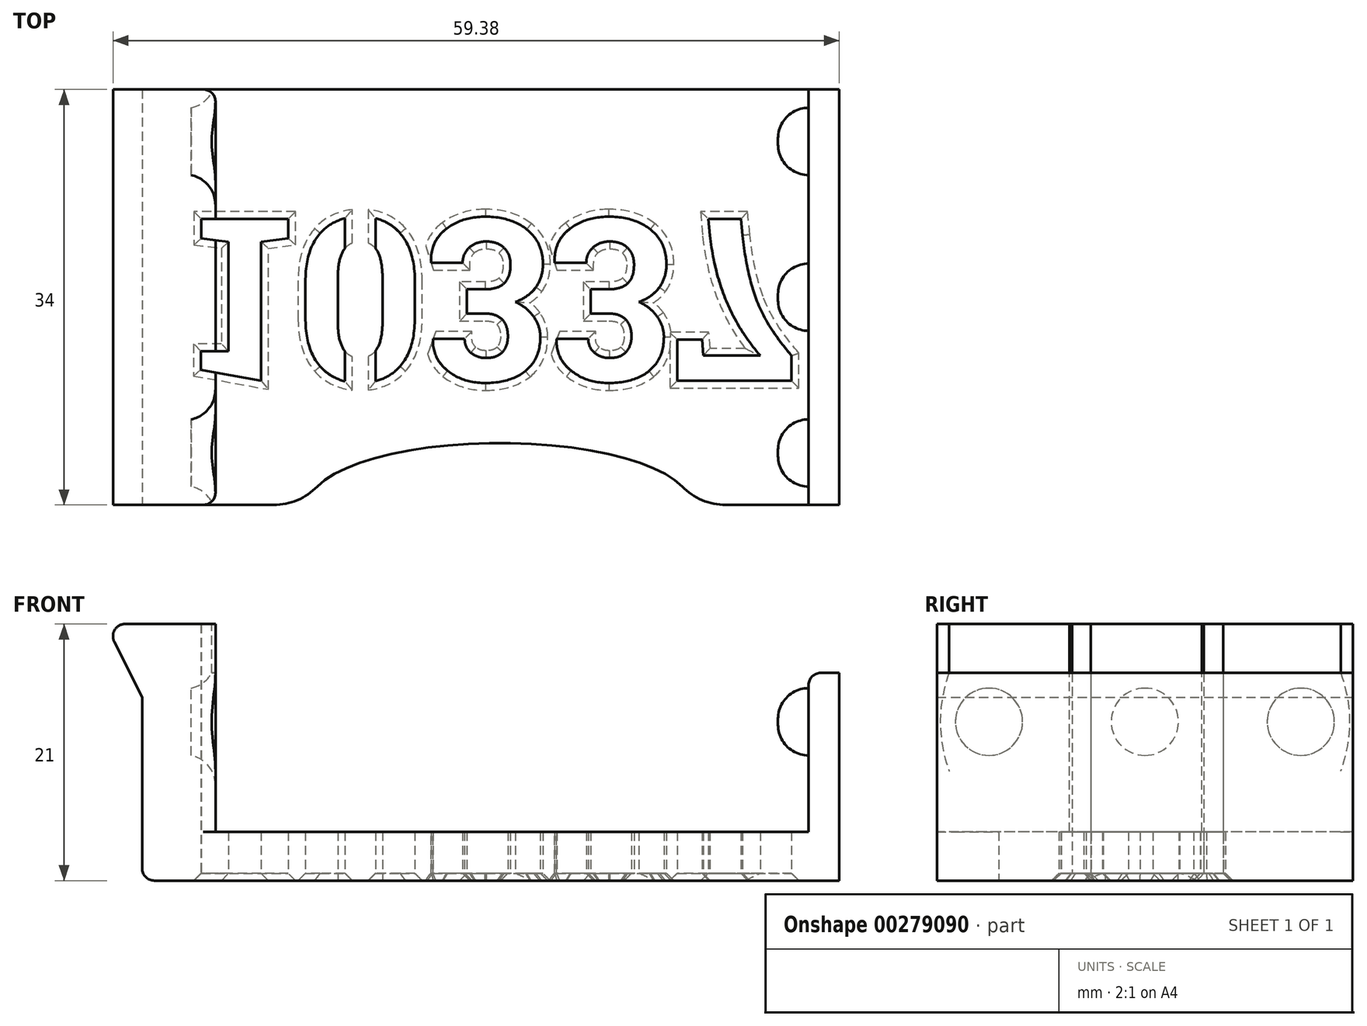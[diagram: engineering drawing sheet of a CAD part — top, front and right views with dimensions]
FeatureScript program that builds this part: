
annotation { "Feature Type Name" : "Feature", "Feature Type Description" : "" }
export const myFeature = defineFeature(function(context is Context, id is Id, definition is map)
    precondition{}
    {
        {
            var Q0;
            Q0=qCreatedBy(makeId("Top.planeOp"),FACE);
            var sketch = newSketch(context, id + "F0", { "sketchPlane" : qUnion([Q0])});
            skLineSegment(sketch, "E0.bottom", {"start": v(-29.25, 25.5) * mm, "end": v(29.25, 25.5) * mm});
            skLineSegment(sketch, "E0.top", {"start": v(-29.25, -25.5) * mm, "end": v(29.25, -25.5) * mm});
            skLineSegment(sketch, "E0.left", {"start": v(-29.25, 25.5) * mm, "end": v(-29.25, -25.5) * mm});
            skLineSegment(sketch, "E0.right", {"start": v(29.25, 25.5) * mm, "end": v(29.25, -25.5) * mm});
            skPoint(sketch, "E0.middle", {"position": v(0, 0) * mm});
            skSolve(sketch);
        }
        {
            var Q0;
            Q0 = qSketchRegion(id + "F0", true);
            extrude(context, id + "F1", {"entities" : qUnion([Q0]), "depth" : 4 * mm});
        }
        {
            var Q0;
            Q0=makeQuery(id+"F1.opExtrude","CAP_FACE",FACE,{"disambiguationData":[OSD([sQuery(id+"F0.wireOp",EDGE,"E0.bottom"),sQuery(id+"F0.wireOp",EDGE,"E0.top"),sQuery(id+"F0.wireOp",EDGE,"E0.left"),sQuery(id+"F0.wireOp",EDGE,"E0.right")])],"isStart":false});
            var sketch = newSketch(context, id + "F2", { "sketchPlane" : qUnion([Q0])});
            skLineSegment(sketch, "E1.bottom", {"start": v(-25.25, 25.5) * mm, "end": v(25.25, 25.5) * mm});
            skLineSegment(sketch, "E1.top", {"start": v(-25.25, -25.5) * mm, "end": v(25.25, -25.5) * mm});
            skLineSegment(sketch, "E1.left", {"start": v(-25.25, 25.5) * mm, "end": v(-25.25, -25.5) * mm});
            skLineSegment(sketch, "E1.right", {"start": v(25.25, 25.5) * mm, "end": v(25.25, -25.5) * mm});
            skPoint(sketch, "E1.middle", {"position": v(0, 0) * mm});
            skSolve(sketch);
        }
        {
            var Q0;
            {var subQ0=sQuery(id+"F2.wireOp",EDGE,"E1.left");Q0=makeQuery(id+"F2.imprint","IMPRINT",FACE,{"disambiguationData":[TD([[makeQuery(id+"F2.imprint","IMPRINT",EDGE,{"derivedFrom":subQ0}),-1.0]])]});}
            var Q1;
            {var subQ0=sQuery(id+"F2.wireOp",EDGE,"E1.right");Q1=makeQuery(id+"F2.imprint","IMPRINT",FACE,{"disambiguationData":[TD([[makeQuery(id+"F2.imprint","IMPRINT",EDGE,{"derivedFrom":subQ0}),1.0]])]});}
            extrude(context, id + "F3", {"entities" : qUnion([Q0, Q1]), "operationType" : NewBodyOperationType.ADD, "depth" : 13 * mm});
        }
        {
            var Q0;
            Q0=makeQuery(id+"F3.opExtrude","SWEPT_FACE",FACE,{"disambiguationData":[OSD([sQuery(id+"F2.wireOp",EDGE,"E1.left")])]});
            var sketch = newSketch(context, id + "F4", { "sketchPlane" : qUnion([Q0])});
            skLineSegment(sketch, "E2", {"start": v(0, 4) * mm, "end": v(0, 13) * mm});
            skPoint(sketch, "E2.endSnap0", {"position": v(0, 4) * mm});
            skLineSegment(sketch, "E3", {"start": v(0, 13) * mm, "end": v(25.5, 13) * mm});
            skLineSegment(sketch, "E4", {"start": v(0, 13) * mm, "end": v(-25.5, 13) * mm});
            skCircle(sketch, "E5", {"center": v(12.75, 13) * mm, "radius": 2.75 * mm});
            skCircle(sketch, "E6", {"center": v(0, 13) * mm, "radius": 2.75 * mm});
            skCircle(sketch, "E7", {"center": v(-12.75, 13) * mm, "radius": 2.75 * mm});
            skSolve(sketch);
        }
        {
            var Q0;
            {var subQ0=sQuery(id+"F4.wireOp",EDGE,"E5");var subQ1=sQuery(id+"F4.wireOp",EDGE,"E3");var subQ2=makeQuery(id+"F4.imprint","INTERSECT",VERTEX,{"disambiguationData":[OD(0.0)],"derivedFrom":[subQ1,subQ0]});Q0=makeQuery(id+"F4.imprint","IMPRINT",FACE,{"disambiguationData":[TD([[makeQuery(id+"F4.imprint","IMPRINT",EDGE,{"disambiguationData":[TD([[subQ2,-1.0]])],"derivedFrom":subQ1}),1.0]])]});}
            var Q1;
            {var subQ0=sQuery(id+"F4.wireOp",EDGE,"E5");var subQ1=sQuery(id+"F4.wireOp",EDGE,"E3");var subQ2=makeQuery(id+"F4.imprint","INTERSECT",VERTEX,{"disambiguationData":[OD(0.0)],"derivedFrom":[subQ1,subQ0]});Q1=makeQuery(id+"F4.imprint","IMPRINT",FACE,{"disambiguationData":[TD([[makeQuery(id+"F4.imprint","IMPRINT",EDGE,{"disambiguationData":[TD([[subQ2,-1.0]])],"derivedFrom":subQ1}),-1.0]])]});}
            var Q2;
            {var subQ1=sQuery(id+"F4.wireOp",EDGE,"E2");var subQ3=sQuery(id+"F4.wireOp",EDGE,"E6");var subQ4=makeQuery(id+"F4.imprint","INTERSECT",VERTEX,{"derivedFrom":[subQ1,subQ3]});Q2=makeQuery(id+"F4.imprint","IMPRINT",FACE,{"disambiguationData":[TD([[makeQuery(id+"F4.imprint","IMPRINT",EDGE,{"disambiguationData":[TD([[subQ4,-1.0]])],"derivedFrom":subQ3}),1.0]])]});}
            var Q3;
            {var subQ1=sQuery(id+"F4.wireOp",EDGE,"E3");var subQ3=sQuery(id+"F4.wireOp",EDGE,"E6");var subQ4=makeQuery(id+"F4.imprint","INTERSECT",VERTEX,{"derivedFrom":[subQ1,subQ3]});Q3=makeQuery(id+"F4.imprint","IMPRINT",FACE,{"disambiguationData":[TD([[makeQuery(id+"F4.imprint","IMPRINT",EDGE,{"disambiguationData":[TD([[subQ4,-1.0]])],"derivedFrom":subQ3}),1.0]])]});}
            var Q4;
            {var subQ1=sQuery(id+"F4.wireOp",EDGE,"E2");var subQ3=sQuery(id+"F4.wireOp",EDGE,"E6");var subQ4=makeQuery(id+"F4.imprint","INTERSECT",VERTEX,{"derivedFrom":[subQ1,subQ3]});Q4=makeQuery(id+"F4.imprint","IMPRINT",FACE,{"disambiguationData":[TD([[makeQuery(id+"F4.imprint","IMPRINT",EDGE,{"disambiguationData":[TD([[subQ4,1.0]])],"derivedFrom":subQ3}),1.0]])]});}
            var Q5;
            {var subQ0=sQuery(id+"F4.wireOp",EDGE,"E7");var subQ1=sQuery(id+"F4.wireOp",EDGE,"E4");var subQ2=makeQuery(id+"F4.imprint","INTERSECT",VERTEX,{"disambiguationData":[OD(0.0)],"derivedFrom":[subQ1,subQ0]});Q5=makeQuery(id+"F4.imprint","IMPRINT",FACE,{"disambiguationData":[TD([[makeQuery(id+"F4.imprint","IMPRINT",EDGE,{"disambiguationData":[TD([[subQ2,-1.0]])],"derivedFrom":subQ1}),1.0]])]});}
            var Q6;
            {var subQ0=sQuery(id+"F4.wireOp",EDGE,"E7");var subQ1=sQuery(id+"F4.wireOp",EDGE,"E4");var subQ2=makeQuery(id+"F4.imprint","INTERSECT",VERTEX,{"disambiguationData":[OD(0.0)],"derivedFrom":[subQ1,subQ0]});Q6=makeQuery(id+"F4.imprint","IMPRINT",FACE,{"disambiguationData":[TD([[makeQuery(id+"F4.imprint","IMPRINT",EDGE,{"disambiguationData":[TD([[subQ2,-1.0]])],"derivedFrom":subQ1}),-1.0]])]});}
            extrude(context, id + "F5", {"entities" : qUnion([Q0, Q1, Q2, Q3, Q4, Q5, Q6]), "operationType" : NewBodyOperationType.ADD, "depth" : 2 * mm});
        }
        {
            var Q0;
            Q0=makeQuery(id+"F3.opExtrude","SWEPT_FACE",FACE,{"disambiguationData":[OSD([sQuery(id+"F2.wireOp",EDGE,"E1.right")])]});
            var sketch = newSketch(context, id + "F6", { "sketchPlane" : qUnion([Q0])});
            skLineSegment(sketch, "E8", {"start": v(0, 4) * mm, "end": v(0, 13) * mm});
            skPoint(sketch, "E8.endSnap0", {"position": v(0, 4) * mm});
            skLineSegment(sketch, "E9", {"start": v(0, 13) * mm, "end": v(25.5, 13) * mm});
            skLineSegment(sketch, "E10", {"start": v(0, 13) * mm, "end": v(-25.5, 13) * mm});
            skCircle(sketch, "E11", {"center": v(0, 13) * mm, "radius": 2.75 * mm});
            skCircle(sketch, "E12", {"center": v(12.75, 13) * mm, "radius": 2.75 * mm});
            skCircle(sketch, "E13", {"center": v(-12.75, 13) * mm, "radius": 2.75 * mm});
            skSolve(sketch);
        }
        {
            var Q0;
            Q0 = qSketchRegion(id + "F6", true);
            extrude(context, id + "F7", {"entities" : qUnion([Q0]), "operationType" : NewBodyOperationType.ADD, "depth" : 2.5 * mm});
        }
        {
            var Q0;
            Q0=makeQuery(id+"F5.opExtrude","CAP_EDGE",EDGE,{"disambiguationData":[OSD([sQuery(id+"F4.wireOp",EDGE,"E5")])],"isStart":false});
            var Q1;
            Q1=makeQuery(id+"F5.opExtrude","CAP_EDGE",EDGE,{"disambiguationData":[OSD([sQuery(id+"F4.wireOp",EDGE,"E6")])],"isStart":false});
            var Q2;
            Q2=makeQuery(id+"F5.opExtrude","CAP_EDGE",EDGE,{"disambiguationData":[OSD([sQuery(id+"F4.wireOp",EDGE,"E7")])],"isStart":false});
            var Q3;
            Q3=makeQuery(id+"F7.opExtrude","CAP_FACE",FACE,{"disambiguationData":[OSD([sQuery(id+"F6.wireOp",EDGE,"E12")])],"isStart":false});
            var Q4;
            Q4=makeQuery(id+"F7.opExtrude","CAP_FACE",FACE,{"disambiguationData":[OSD([sQuery(id+"F6.wireOp",EDGE,"E11")])],"isStart":false});
            var Q5;
            Q5=makeQuery(id+"F7.opExtrude","CAP_FACE",FACE,{"disambiguationData":[OSD([sQuery(id+"F6.wireOp",EDGE,"E13")])],"isStart":false});
            fillet(context, id + "F8", {"entities" : qUnion([Q0, Q1, Q2, Q3, Q4, Q5]), "radius" : 2.5 * mm, "tangentPropagation" : true, "allowEdgeOverflow" : false});
        }
        {
            var Q0;
            {var subQ0=sQuery(id+"F0.wireOp",EDGE,"E0.top");var subQ1=makeQuery(id+"F1.opExtrude","CAP_EDGE",EDGE,{"disambiguationData":[OSD([subQ0])],"isStart":false});Q0=makeQuery(id+"F3.boolean.opBoolean","MERGE",FACE,{"derivedFrom":[makeQuery(id+"F1.opExtrude","SWEPT_FACE",FACE,{"disambiguationData":[OSD([subQ0])]}),makeQuery(id+"F3.opExtrude","SWEPT_FACE",FACE,{"disambiguationData":[OSD([subQ0]),TDD([makeQuery(id+"F2.imprint","IMPRINT",EDGE,{"disambiguationData":[TD([[makeQuery(id+"F2.imprint","INTERSECT",VERTEX,{"derivedFrom":[subQ1,makeQuery(id+"F1.opExtrude","CAP_EDGE",EDGE,{"disambiguationData":[OSD([sQuery(id+"F0.wireOp",EDGE,"E0.left")])],"isStart":false})]}),-1.0]])],"derivedFrom":subQ1})])]}),makeQuery(id+"F3.opExtrude","SWEPT_FACE",FACE,{"disambiguationData":[OSD([subQ0]),TDD([makeQuery(id+"F2.imprint","IMPRINT",EDGE,{"disambiguationData":[TD([[makeQuery(id+"F2.imprint","INTERSECT",VERTEX,{"derivedFrom":[subQ1,makeQuery(id+"F1.opExtrude","CAP_EDGE",EDGE,{"disambiguationData":[OSD([sQuery(id+"F0.wireOp",EDGE,"E0.right")])],"isStart":false})]}),1.0]])],"derivedFrom":subQ1})])]})]});}
            var sketch = newSketch(context, id + "F9", { "sketchPlane" : qUnion([Q0])});
            skLineSegment(sketch, "E14.bottom", {"start": v(29.25, 17) * mm, "end": v(27.75, 17) * mm});
            skLineSegment(sketch, "E14.top", {"start": v(29.25, 0) * mm, "end": v(27.75, 0) * mm});
            skLineSegment(sketch, "E14.left", {"start": v(29.25, 17) * mm, "end": v(29.25, 0) * mm});
            skLineSegment(sketch, "E14.right", {"start": v(27.75, 17) * mm, "end": v(27.75, 0) * mm});
            skSolve(sketch);
        }
        {
            var Q0;
            Q0 = qSketchRegion(id + "F9", true);
            extrude(context, id + "F10", {"entities" : qUnion([Q0]), "operationType" : NewBodyOperationType.REMOVE, "endBound" : BoundingType.THROUGH_ALL, "oppositeDirection" : true, "depth" : 25 * mm});
        }
        {
            var Q0;
            Q0=makeQuery(id+"F3.opExtrude","CAP_FACE",FACE,{"disambiguationData":[OSD([sQuery(id+"F0.wireOp",EDGE,"E0.bottom"),sQuery(id+"F0.wireOp",EDGE,"E0.top"),sQuery(id+"F0.wireOp",EDGE,"E0.left"),sQuery(id+"F2.wireOp",EDGE,"E1.left")])],"isStart":false});
            extrude(context, id + "F11", {"entities" : qUnion([Q0]), "operationType" : NewBodyOperationType.ADD, "depth" : 4 * mm});
        }
        {
            var Q0;
            {var subQ0=sQuery(id+"F0.wireOp",EDGE,"E0.left");Q0=makeQuery(id+"F11.boolean.opBoolean","MERGE",FACE,{"derivedFrom":[makeQuery(id+"F3.boolean.opBoolean","MERGE",FACE,{"derivedFrom":[makeQuery(id+"F1.opExtrude","SWEPT_FACE",FACE,{"disambiguationData":[OSD([subQ0])]}),makeQuery(id+"F3.opExtrude","SWEPT_FACE",FACE,{"disambiguationData":[OSD([subQ0])]})]}),makeQuery(id+"F11.opExtrude","SWEPT_FACE",FACE,{"disambiguationData":[OSD([subQ0])]})]});}
            var sketch = newSketch(context, id + "F12", { "sketchPlane" : qUnion([Q0])});
            skLineSegment(sketch, "E15.bottom", {"start": v(25.5, 21) * mm, "end": v(-25.5, 21) * mm});
            skLineSegment(sketch, "E15.top", {"start": v(25.5, 15) * mm, "end": v(-25.5, 15) * mm});
            skLineSegment(sketch, "E15.left", {"start": v(25.5, 21) * mm, "end": v(25.5, 15) * mm});
            skLineSegment(sketch, "E15.right", {"start": v(-25.5, 21) * mm, "end": v(-25.5, 15) * mm});
            skSolve(sketch);
        }
        {
            var Q0;
            Q0 = qSketchRegion(id + "F12", true);
            extrude(context, id + "F13", {"entities" : qUnion([Q0]), "operationType" : NewBodyOperationType.ADD, "depth" : 3 * mm});
        }
        {
            var Q0;
            {var subQ0=sQuery(id+"F0.wireOp",EDGE,"E0.top");var subQ1=makeQuery(id+"F1.opExtrude","CAP_EDGE",EDGE,{"disambiguationData":[OSD([subQ0])],"isStart":false});Q0=makeQuery(id+"F13.boolean.opBoolean","MERGE",FACE,{"derivedFrom":[makeQuery(id+"F11.boolean.opBoolean","MERGE",FACE,{"derivedFrom":[makeQuery(id+"F3.boolean.opBoolean","MERGE",FACE,{"derivedFrom":[makeQuery(id+"F1.opExtrude","SWEPT_FACE",FACE,{"disambiguationData":[OSD([subQ0])]}),makeQuery(id+"F3.opExtrude","SWEPT_FACE",FACE,{"disambiguationData":[OSD([subQ0]),TDD([makeQuery(id+"F2.imprint","IMPRINT",EDGE,{"disambiguationData":[TD([[makeQuery(id+"F2.imprint","INTERSECT",VERTEX,{"derivedFrom":[subQ1,makeQuery(id+"F1.opExtrude","CAP_EDGE",EDGE,{"disambiguationData":[OSD([sQuery(id+"F0.wireOp",EDGE,"E0.left")])],"isStart":false})]}),-1.0]])],"derivedFrom":subQ1})])]}),makeQuery(id+"F3.opExtrude","SWEPT_FACE",FACE,{"disambiguationData":[OSD([subQ0]),TDD([makeQuery(id+"F2.imprint","IMPRINT",EDGE,{"disambiguationData":[TD([[makeQuery(id+"F2.imprint","INTERSECT",VERTEX,{"derivedFrom":[subQ1,makeQuery(id+"F1.opExtrude","CAP_EDGE",EDGE,{"disambiguationData":[OSD([sQuery(id+"F0.wireOp",EDGE,"E0.right")])],"isStart":false})]}),1.0]])],"derivedFrom":subQ1})])]})]}),makeQuery(id+"F11.opExtrude","SWEPT_FACE",FACE,{"disambiguationData":[OSD([subQ0])]})]}),makeQuery(id+"F13.opExtrude","SWEPT_FACE",FACE,{"disambiguationData":[OSD([sQuery(id+"F12.wireOp",EDGE,"E15.left")])]})]});}
            var sketch = newSketch(context, id + "F14", { "sketchPlane" : qUnion([Q0])});
            skLineSegment(sketch, "E16", {"start": v(-32.25, 21) * mm, "end": v(-29.25, 15) * mm});
            skLineSegment(sketch, "E17", {"start": v(-32.25, 21) * mm, "end": v(-25.25, 18) * mm});
            skPoint(sketch, "E17.endSnap0", {"position": v(-30.75, 18) * mm});
            skSolve(sketch);
        }
        {
            var Q0;
            Q0=makeQuery(id+"F14.imprint","IMPRINT",FACE,{"disambiguationData":[TD([[makeQuery(id+"F14.imprint","IMPRINT",EDGE,{"derivedFrom":sQuery(id+"F14.wireOp",EDGE,"E16")}),-1.0]])]});
            var Q1;
            {var subQ0=sQuery(id+"F14.wireOp",EDGE,"E17");Q1=makeQuery(id+"F14.imprint","IMPRINT",FACE,{"disambiguationData":[TD([[makeQuery(id+"F14.imprint","IMPRINT",EDGE,{"derivedFrom":subQ0}),1.0]])]});}
            extrude(context, id + "F15", {"entities" : qUnion([Q0, Q1]), "operationType" : NewBodyOperationType.REMOVE, "endBound" : BoundingType.THROUGH_ALL, "oppositeDirection" : true, "depth" : 25 * mm});
        }
        {
            var Q0;
            {var subQ0=sQuery(id+"F0.wireOp",EDGE,"E0.top");var subQ1=makeQuery(id+"F1.opExtrude","CAP_EDGE",EDGE,{"disambiguationData":[OSD([subQ0])],"isStart":false});Q0=makeQuery(id+"F13.boolean.opBoolean","MERGE",FACE,{"derivedFrom":[makeQuery(id+"F11.boolean.opBoolean","MERGE",FACE,{"derivedFrom":[makeQuery(id+"F3.boolean.opBoolean","MERGE",FACE,{"derivedFrom":[makeQuery(id+"F1.opExtrude","SWEPT_FACE",FACE,{"disambiguationData":[OSD([subQ0])]}),makeQuery(id+"F3.opExtrude","SWEPT_FACE",FACE,{"disambiguationData":[OSD([subQ0]),TDD([makeQuery(id+"F2.imprint","IMPRINT",EDGE,{"disambiguationData":[TD([[makeQuery(id+"F2.imprint","INTERSECT",VERTEX,{"derivedFrom":[subQ1,makeQuery(id+"F1.opExtrude","CAP_EDGE",EDGE,{"disambiguationData":[OSD([sQuery(id+"F0.wireOp",EDGE,"E0.left")])],"isStart":false})]}),-1.0]])],"derivedFrom":subQ1})])]}),makeQuery(id+"F3.opExtrude","SWEPT_FACE",FACE,{"disambiguationData":[OSD([subQ0]),TDD([makeQuery(id+"F2.imprint","IMPRINT",EDGE,{"disambiguationData":[TD([[makeQuery(id+"F2.imprint","INTERSECT",VERTEX,{"derivedFrom":[subQ1,makeQuery(id+"F1.opExtrude","CAP_EDGE",EDGE,{"disambiguationData":[OSD([sQuery(id+"F0.wireOp",EDGE,"E0.right")])],"isStart":false})]}),1.0]])],"derivedFrom":subQ1})])]})]}),makeQuery(id+"F11.opExtrude","SWEPT_FACE",FACE,{"disambiguationData":[OSD([subQ0])]})]}),makeQuery(id+"F13.opExtrude","SWEPT_FACE",FACE,{"disambiguationData":[OSD([sQuery(id+"F12.wireOp",EDGE,"E15.left")])]})]});}
            extrude(context, id + "F16", {"entities" : qUnion([Q0]), "operationType" : NewBodyOperationType.REMOVE, "oppositeDirection" : true, "depth" : 8.5 * mm});
        }
        {
            var Q0;
            {var subQ0=sQuery(id+"F0.wireOp",EDGE,"E0.bottom");var subQ1=makeQuery(id+"F1.opExtrude","CAP_EDGE",EDGE,{"disambiguationData":[OSD([subQ0])],"isStart":false});Q0=makeQuery(id+"F13.boolean.opBoolean","MERGE",FACE,{"derivedFrom":[makeQuery(id+"F11.boolean.opBoolean","MERGE",FACE,{"derivedFrom":[makeQuery(id+"F3.boolean.opBoolean","MERGE",FACE,{"derivedFrom":[makeQuery(id+"F1.opExtrude","SWEPT_FACE",FACE,{"disambiguationData":[OSD([subQ0])]}),makeQuery(id+"F3.opExtrude","SWEPT_FACE",FACE,{"disambiguationData":[OSD([subQ0]),TDD([makeQuery(id+"F2.imprint","IMPRINT",EDGE,{"disambiguationData":[TD([[makeQuery(id+"F2.imprint","INTERSECT",VERTEX,{"derivedFrom":[subQ1,makeQuery(id+"F1.opExtrude","CAP_EDGE",EDGE,{"disambiguationData":[OSD([sQuery(id+"F0.wireOp",EDGE,"E0.left")])],"isStart":false})]}),-1.0]])],"derivedFrom":subQ1})])]}),makeQuery(id+"F3.opExtrude","SWEPT_FACE",FACE,{"disambiguationData":[OSD([subQ0]),TDD([makeQuery(id+"F2.imprint","IMPRINT",EDGE,{"disambiguationData":[TD([[makeQuery(id+"F2.imprint","INTERSECT",VERTEX,{"derivedFrom":[subQ1,makeQuery(id+"F1.opExtrude","CAP_EDGE",EDGE,{"disambiguationData":[OSD([sQuery(id+"F0.wireOp",EDGE,"E0.right")])],"isStart":false})]}),1.0]])],"derivedFrom":subQ1})])]})]}),makeQuery(id+"F11.opExtrude","SWEPT_FACE",FACE,{"disambiguationData":[OSD([subQ0])]})]}),makeQuery(id+"F13.opExtrude","SWEPT_FACE",FACE,{"disambiguationData":[OSD([sQuery(id+"F12.wireOp",EDGE,"E15.right")])]})]});}
            extrude(context, id + "F17", {"entities" : qUnion([Q0]), "operationType" : NewBodyOperationType.REMOVE, "oppositeDirection" : true, "depth" : 8.5 * mm});
        }
        {
            var Q0;
            {var subQ0=sQuery(id+"F24.wireOp",EDGE,"E21.right");var subQ1=sQuery(id+"F24.wireOp",EDGE,"E21.left");var subQ2=sQuery(id+"F22.wireOp",EDGE,"E19.sketch_text.stroke-27");var subQ3=sQuery(id+"F22.wireOp",EDGE,"E19.sketch_text.stroke-26");var subQ4=sQuery(id+"F22.wireOp",EDGE,"E19.sketch_text.stroke-22");var subQ5=sQuery(id+"F22.wireOp",EDGE,"E19.sketch_text.stroke-21");var subQ7=sQuery(id+"F2.wireOp",EDGE,"E1.left");var subQ9=sQuery(id+"F0.wireOp",EDGE,"E0.bottom");var subQ10=sQuery(id+"F0.wireOp",EDGE,"E0.top");var subQ12=makeQuery(id+"F1.opExtrude","CAP_FACE",FACE,{"disambiguationData":[OSD([subQ9,subQ10,sQuery(id+"F0.wireOp",EDGE,"E0.left"),sQuery(id+"F0.wireOp",EDGE,"E0.right")])],"isStart":false});Q0=makeQuery(id+"F25.boolean.opBoolean","MERGE",FACE,{"derivedFrom":[makeQuery(id+"F23.boolean.opBoolean","SPLIT",FACE,{"disambiguationData":[TD([makeQuery(id+"F23.opExtrude","SWEPT_FACE",FACE,{"disambiguationData":[OSD([sQuery(id+"F22.wireOp",EDGE,"E19.sketch_text.stroke-20")])]})])],"derivedFrom":subQ12}),makeQuery(id+"F23.boolean.opBoolean","SPLIT",FACE,{"disambiguationData":[TD([makeQuery(id+"F3.opExtrude","SWEPT_FACE",FACE,{"disambiguationData":[OSD([subQ7])]})])],"derivedFrom":subQ12}),makeQuery(id+"F25.opExtrude","CAP_FACE",FACE,{"disambiguationData":[OSD([subQ5,subQ4,sQuery(id+"F24.wireOp",EDGE,"E21.bottom"),subQ1,subQ0])],"isStart":false}),makeQuery(id+"F25.opExtrude","CAP_FACE",FACE,{"disambiguationData":[OSD([subQ3,subQ2,sQuery(id+"F24.wireOp",EDGE,"E21.top"),subQ1,subQ0])],"isStart":false})]});}
            var sketch = newSketch(context, id + "F18", { "sketchPlane" : qUnion([Q0])});
            skEllipse(sketch, "E18", {"center": v(0, -17.04) * mm, "majorRadius": 15.65 * mm, "minorRadius": 5.1 * mm, "majorAxis": v(1, 0)});
            skSolve(sketch);
        }
        {
            var Q0;
            Q0 = qSketchRegion(id + "F18", true);
            var Q1;
            {var subQ0=sQuery(id+"F18.wireOp",EDGE,"E18");var subQ1=sQuery(id+"F0.wireOp",EDGE,"E0.top");var subQ2=makeQuery(id+"F21.opFillet","BLEND_EDGE",EDGE,{"blendedFrom":[makeQuery(id+"F16.boolean.opBoolean","COPY",EDGE,{"derivedFrom":makeQuery(id+"F16.opExtrude","CAP_EDGE",EDGE,{"disambiguationData":[OSD([subQ1]),TDD([makeQuery(id+"F1.opExtrude","CAP_EDGE",EDGE,{"disambiguationData":[OSD([subQ1])],"isStart":false})])],"isStart":false})}),makeQuery(id+"F1.opExtrude","CAP_FACE",FACE,{"disambiguationData":[OSD([sQuery(id+"F0.wireOp",EDGE,"E0.bottom"),subQ1,sQuery(id+"F0.wireOp",EDGE,"E0.left"),sQuery(id+"F0.wireOp",EDGE,"E0.right")])],"isStart":false})],"blendedInto":[makeQuery(id+"F1.opExtrude","CAP_FACE",FACE,{"disambiguationData":[OSD([sQuery(id+"F0.wireOp",EDGE,"E0.bottom"),subQ1,sQuery(id+"F0.wireOp",EDGE,"E0.left"),sQuery(id+"F0.wireOp",EDGE,"E0.right")])],"isStart":false})]});var subQ3=makeQuery(id+"F18.imprint","INTERSECT",VERTEX,{"disambiguationData":[OD(0.0)],"derivedFrom":[subQ2,subQ0]});Q1=makeQuery(id+"F18.imprint","IMPRINT",FACE,{"disambiguationData":[TD([[makeQuery(id+"F18.imprint","IMPRINT",EDGE,{"disambiguationData":[TD([[subQ3,-1.0]])],"derivedFrom":subQ0}),1.0]])]});}
            extrude(context, id + "F19", {"entities" : qUnion([Q0, Q1]), "operationType" : NewBodyOperationType.REMOVE, "oppositeDirection" : true, "depth" : 25 * mm});
        }
        {
            var Q0;
            Q0=makeQuery(id+"F19.boolean.opBoolean","INTERSECT",EDGE,{"disambiguationData":[OD(1.0)],"derivedFrom":[makeQuery(id+"F16.boolean.opBoolean","COPY",FACE,{"derivedFrom":makeQuery(id+"F16.opExtrude","CAP_FACE",FACE,{"disambiguationData":[OSD([sQuery(id+"F0.wireOp",EDGE,"E0.top"),sQuery(id+"F12.wireOp",EDGE,"E15.left")])],"isStart":false})}),makeQuery(id+"F19.opExtrude","SWEPT_FACE",FACE,{"disambiguationData":[OSD([sQuery(id+"F18.wireOp",EDGE,"E18")])]})]});
            var Q1;
            Q1=makeQuery(id+"F19.boolean.opBoolean","INTERSECT",EDGE,{"disambiguationData":[OD(0.0)],"derivedFrom":[makeQuery(id+"F16.boolean.opBoolean","COPY",FACE,{"derivedFrom":makeQuery(id+"F16.opExtrude","CAP_FACE",FACE,{"disambiguationData":[OSD([sQuery(id+"F0.wireOp",EDGE,"E0.top"),sQuery(id+"F12.wireOp",EDGE,"E15.left")])],"isStart":false})}),makeQuery(id+"F19.opExtrude","SWEPT_FACE",FACE,{"disambiguationData":[OSD([sQuery(id+"F18.wireOp",EDGE,"E18")])]})]});
            fillet(context, id + "F20", {"entities" : qUnion([Q0, Q1]), "radius" : 5 * mm, "tangentPropagation" : true, "allowEdgeOverflow" : false});
        }
        {
            var Q0;
            {var subQ0=sQuery(id+"F14.wireOp",EDGE,"E17");var subQ1=sQuery(id+"F12.wireOp",EDGE,"E15.left");var subQ2=sQuery(id+"F12.wireOp",EDGE,"E15.bottom");var subQ3=sQuery(id+"F0.wireOp",EDGE,"E0.top");var subQ4=sQuery(id+"F14.wireOp",EDGE,"E16");Q0=makeQuery(id+"F15.boolean.opBoolean","MERGE",EDGE,{"derivedFrom":[makeQuery(id+"F13.opExtrude","CAP_EDGE",EDGE,{"disambiguationData":[OSD([subQ2])],"isStart":false}),makeQuery(id+"F15.opExtrude","SWEPT_EDGE",EDGE,{"disambiguationData":[OSD([subQ3,subQ2,subQ1,subQ4,subQ0]),ownerDisambiguation([makeQuery(id+"F15.opExtrude","SWEPT_BODY",BODY,{"disambiguationData":[OSD([subQ3,sQuery(id+"F0.wireOp",EDGE,"E0.left"),sQuery(id+"F12.wireOp",EDGE,"E15.top"),subQ1,subQ4])]})])]}),makeQuery(id+"F15.opExtrude","SWEPT_EDGE",EDGE,{"disambiguationData":[OSD([subQ3,subQ2,subQ1,subQ4,subQ0]),ownerDisambiguation([makeQuery(id+"F15.opExtrude","SWEPT_BODY",BODY,{"disambiguationData":[OSD([subQ3,sQuery(id+"F2.wireOp",EDGE,"E1.top"),sQuery(id+"F2.wireOp",EDGE,"E1.left"),subQ2,subQ1,subQ0])]})])]})]});}
            var Q1;
            Q1=makeQuery(id+"F15.boolean.opBoolean","COPY",EDGE,{"derivedFrom":makeQuery(id+"F15.opExtrude","SWEPT_EDGE",EDGE,{"disambiguationData":[OSD([sQuery(id+"F0.wireOp",EDGE,"E0.top"),sQuery(id+"F2.wireOp",EDGE,"E1.top"),sQuery(id+"F2.wireOp",EDGE,"E1.left"),sQuery(id+"F14.wireOp",EDGE,"E17")])]})});
            var Q2;
            Q2=makeQuery(id+"F3.opExtrude","CAP_EDGE",EDGE,{"disambiguationData":[OSD([sQuery(id+"F2.wireOp",EDGE,"E1.right")])],"isStart":false});
            var Q3;
            Q3=makeQuery(id+"F10.boolean.opBoolean","COPY",EDGE,{"derivedFrom":makeQuery(id+"F10.opExtrude","SWEPT_EDGE",EDGE,{"disambiguationData":[OSD([sQuery(id+"F0.wireOp",EDGE,"E0.top"),sQuery(id+"F9.wireOp",EDGE,"E14.bottom"),sQuery(id+"F9.wireOp",EDGE,"E14.right")])]})});
            var Q4;
            Q4=makeQuery(id+"F1.opExtrude","CAP_EDGE",EDGE,{"disambiguationData":[OSD([sQuery(id+"F0.wireOp",EDGE,"E0.left")])],"isStart":true});
            var Q5;
            Q5=makeQuery(id+"F10.boolean.opBoolean","COPY",EDGE,{"derivedFrom":makeQuery(id+"F10.opExtrude","SWEPT_EDGE",EDGE,{"disambiguationData":[OSD([sQuery(id+"F0.wireOp",EDGE,"E0.top"),sQuery(id+"F9.wireOp",EDGE,"E14.top"),sQuery(id+"F9.wireOp",EDGE,"E14.right")])]})});
            var Q6;
            Q6=makeQuery(id+"F1.opExtrude","CAP_EDGE",EDGE,{"disambiguationData":[OSD([sQuery(id+"F0.wireOp",EDGE,"E0.bottom")])],"isStart":true});
            var Q7;
            Q7=makeQuery(id+"F1.opExtrude","CAP_EDGE",EDGE,{"disambiguationData":[OSD([sQuery(id+"F0.wireOp",EDGE,"E0.top")])],"isStart":true});
            var Q8;
            {var subQ0=sQuery(id+"F0.wireOp",EDGE,"E0.bottom");Q8=makeQuery(id+"F17.boolean.opBoolean","COPY",EDGE,{"derivedFrom":makeQuery(id+"F17.opExtrude","CAP_EDGE",EDGE,{"disambiguationData":[OSD([subQ0]),TDD([makeQuery(id+"F1.opExtrude","CAP_EDGE",EDGE,{"disambiguationData":[OSD([subQ0])],"isStart":true})])],"isStart":false})});}
            var Q9;
            {var subQ0=sQuery(id+"F0.wireOp",EDGE,"E0.top");Q9=makeQuery(id+"F16.boolean.opBoolean","COPY",EDGE,{"derivedFrom":makeQuery(id+"F16.opExtrude","CAP_EDGE",EDGE,{"disambiguationData":[OSD([subQ0]),TDD([makeQuery(id+"F1.opExtrude","CAP_EDGE",EDGE,{"disambiguationData":[OSD([subQ0])],"isStart":true})])],"isStart":false})});}
            var Q10;
            Q10=makeQuery(id+"F16.boolean.opBoolean","COPY",EDGE,{"derivedFrom":makeQuery(id+"F16.opExtrude","CAP_EDGE",EDGE,{"disambiguationData":[OSD([sQuery(id+"F0.wireOp",EDGE,"E0.top"),sQuery(id+"F0.wireOp",EDGE,"E0.left")])],"isStart":false})});
            var Q11;
            Q11=makeQuery(id+"F16.boolean.opBoolean","COPY",EDGE,{"derivedFrom":makeQuery(id+"F16.opExtrude","CAP_EDGE",EDGE,{"disambiguationData":[OSD([sQuery(id+"F14.wireOp",EDGE,"E16")])],"isStart":false})});
            var Q12;
            Q12=makeQuery(id+"F17.boolean.opBoolean","COPY",EDGE,{"derivedFrom":makeQuery(id+"F17.opExtrude","CAP_EDGE",EDGE,{"disambiguationData":[OSD([sQuery(id+"F0.wireOp",EDGE,"E0.bottom"),sQuery(id+"F12.wireOp",EDGE,"E15.right"),sQuery(id+"F14.wireOp",EDGE,"E16")])],"isStart":false})});
            var Q13;
            Q13=makeQuery(id+"F17.boolean.opBoolean","COPY",EDGE,{"derivedFrom":makeQuery(id+"F17.opExtrude","CAP_EDGE",EDGE,{"disambiguationData":[OSD([sQuery(id+"F0.wireOp",EDGE,"E0.bottom"),sQuery(id+"F0.wireOp",EDGE,"E0.left")])],"isStart":false})});
            var Q14;
            Q14=makeQuery(id+"F17.boolean.opBoolean","COPY",EDGE,{"derivedFrom":makeQuery(id+"F17.opExtrude","CAP_EDGE",EDGE,{"disambiguationData":[OSD([sQuery(id+"F0.wireOp",EDGE,"E0.bottom"),sQuery(id+"F9.wireOp",EDGE,"E14.right")])],"isStart":false})});
            var Q15;
            Q15=makeQuery(id+"F16.boolean.opBoolean","COPY",EDGE,{"derivedFrom":makeQuery(id+"F16.opExtrude","CAP_EDGE",EDGE,{"disambiguationData":[OSD([sQuery(id+"F9.wireOp",EDGE,"E14.right")])],"isStart":false})});
            var Q16;
            Q16=makeQuery(id+"F17.boolean.opBoolean","COPY",EDGE,{"derivedFrom":makeQuery(id+"F17.opExtrude","CAP_EDGE",EDGE,{"disambiguationData":[OSD([sQuery(id+"F0.wireOp",EDGE,"E0.bottom"),sQuery(id+"F12.wireOp",EDGE,"E15.right"),sQuery(id+"F14.wireOp",EDGE,"E17")])],"isStart":false})});
            var Q17;
            Q17=makeQuery(id+"F17.boolean.opBoolean","COPY",EDGE,{"derivedFrom":makeQuery(id+"F17.opExtrude","CAP_EDGE",EDGE,{"disambiguationData":[OSD([sQuery(id+"F0.wireOp",EDGE,"E0.bottom"),sQuery(id+"F2.wireOp",EDGE,"E1.bottom"),sQuery(id+"F2.wireOp",EDGE,"E1.left")])],"isStart":false})});
            var Q18;
            Q18=makeQuery(id+"F16.boolean.opBoolean","COPY",EDGE,{"derivedFrom":makeQuery(id+"F16.opExtrude","CAP_EDGE",EDGE,{"disambiguationData":[OSD([sQuery(id+"F0.wireOp",EDGE,"E0.top"),sQuery(id+"F2.wireOp",EDGE,"E1.top"),sQuery(id+"F2.wireOp",EDGE,"E1.left")])],"isStart":false})});
            var Q19;
            Q19=makeQuery(id+"F16.boolean.opBoolean","COPY",EDGE,{"derivedFrom":makeQuery(id+"F16.opExtrude","CAP_EDGE",EDGE,{"disambiguationData":[OSD([sQuery(id+"F14.wireOp",EDGE,"E17")])],"isStart":false})});
            var Q20;
            Q20=makeQuery(id+"F16.boolean.opBoolean","COPY",EDGE,{"derivedFrom":makeQuery(id+"F16.opExtrude","CAP_EDGE",EDGE,{"disambiguationData":[OSD([sQuery(id+"F0.wireOp",EDGE,"E0.top"),sQuery(id+"F2.wireOp",EDGE,"E1.top"),sQuery(id+"F2.wireOp",EDGE,"E1.right")])],"isStart":false})});
            var Q21;
            {var subQ0=sQuery(id+"F0.wireOp",EDGE,"E0.top");Q21=makeQuery(id+"F16.boolean.opBoolean","COPY",EDGE,{"derivedFrom":makeQuery(id+"F16.opExtrude","CAP_EDGE",EDGE,{"disambiguationData":[OSD([subQ0]),TDD([makeQuery(id+"F1.opExtrude","CAP_EDGE",EDGE,{"disambiguationData":[OSD([subQ0])],"isStart":false})])],"isStart":false})});}
            var Q22;
            {var subQ0=sQuery(id+"F0.wireOp",EDGE,"E0.bottom");Q22=makeQuery(id+"F17.boolean.opBoolean","COPY",EDGE,{"derivedFrom":makeQuery(id+"F17.opExtrude","CAP_EDGE",EDGE,{"disambiguationData":[OSD([subQ0]),TDD([makeQuery(id+"F1.opExtrude","CAP_EDGE",EDGE,{"disambiguationData":[OSD([subQ0])],"isStart":false})])],"isStart":false})});}
            var Q23;
            Q23=makeQuery(id+"F17.boolean.opBoolean","COPY",EDGE,{"derivedFrom":makeQuery(id+"F17.opExtrude","CAP_EDGE",EDGE,{"disambiguationData":[OSD([sQuery(id+"F0.wireOp",EDGE,"E0.bottom"),sQuery(id+"F2.wireOp",EDGE,"E1.bottom"),sQuery(id+"F2.wireOp",EDGE,"E1.right")])],"isStart":false})});
            fillet(context, id + "F21", {"entities" : qUnion([Q0, Q1, Q2, Q3, Q4, Q5, Q6, Q7, Q8, Q9, Q10, Q11, Q12, Q13, Q14, Q15, Q16, Q17, Q18, Q19, Q20, Q21, Q22, Q23]), "radius" : 1 * mm, "tangentPropagation" : true, "allowEdgeOverflow" : false});
        }
        {
            var Q0;
            Q0=makeQuery(id+"F1.opExtrude","CAP_FACE",FACE,{"disambiguationData":[OSD([sQuery(id+"F0.wireOp",EDGE,"E0.bottom"),sQuery(id+"F0.wireOp",EDGE,"E0.top"),sQuery(id+"F0.wireOp",EDGE,"E0.left"),sQuery(id+"F0.wireOp",EDGE,"E0.right")])],"isStart":true});
            var sketch = newSketch(context, id + "F22", { "sketchPlane" : qUnion([Q0])});
            skText(sketch, "E19", { "text": "10337", "fontName": "RobotoSlab-Bold.ttf"});
            const initialGuessF22  = {"E19": [-0.025, -0.0064, 1, 0, 0.0134]};
            skSetInitialGuess(sketch, initialGuessF22);
            skSolve(sketch);
        }
        {
            var Q0;
            Q0 = qSketchRegion(id + "F22", true);
            extrude(context, id + "F23", {"entities" : qUnion([Q0]), "operationType" : NewBodyOperationType.REMOVE, "oppositeDirection" : true, "depth" : 25 * mm});
        }
        {
            var Q0;
            Q0=makeQuery(id+"F23.boolean.opBoolean","SPLIT",FACE,{"disambiguationData":[TD([makeQuery(id+"F23.opExtrude","SWEPT_FACE",FACE,{"disambiguationData":[OSD([sQuery(id+"F22.wireOp",EDGE,"E19.sketch_text.stroke-20")])]})])],"derivedFrom":makeQuery(id+"F1.opExtrude","CAP_FACE",FACE,{"disambiguationData":[OSD([sQuery(id+"F0.wireOp",EDGE,"E0.bottom"),sQuery(id+"F0.wireOp",EDGE,"E0.top"),sQuery(id+"F0.wireOp",EDGE,"E0.left"),sQuery(id+"F0.wireOp",EDGE,"E0.right")])],"isStart":true})});
            var sketch = newSketch(context, id + "F24", { "sketchPlane" : qUnion([Q0])});
            skLineSegment(sketch, "E20", {"start": v(-11.42, 4.98) * mm, "end": v(-11.4, -4.55) * mm});
            skLineSegment(sketch, "E21.bottom", {"start": v(-12.66, 8.1) * mm, "end": v(-10.16, 8.1) * mm});
            skLineSegment(sketch, "E21.top", {"start": v(-12.66, -7.67) * mm, "end": v(-10.16, -7.67) * mm});
            skLineSegment(sketch, "E21.left", {"start": v(-12.66, 8.1) * mm, "end": v(-12.66, -7.67) * mm});
            skLineSegment(sketch, "E21.right", {"start": v(-10.16, 8.1) * mm, "end": v(-10.16, -7.67) * mm});
            skPoint(sketch, "E21.middle", {"position": v(-11.41, 0.21) * mm});
            skSolve(sketch);
        }
        {
            var Q0;
            {var subQ5=sQuery(id+"F24.wireOp",EDGE,"E21.bottom");Q0=makeQuery(id+"F24.imprint","IMPRINT",FACE,{"disambiguationData":[TD([[makeQuery(id+"F24.imprint","IMPRINT",EDGE,{"derivedFrom":subQ5}),-1.0]])]});}
            var Q1;
            {var subQ6=sQuery(id+"F24.wireOp",EDGE,"E21.top");Q1=makeQuery(id+"F24.imprint","IMPRINT",FACE,{"disambiguationData":[TD([[makeQuery(id+"F24.imprint","IMPRINT",EDGE,{"derivedFrom":subQ6}),1.0]])]});}
            extrude(context, id + "F25", {"entities" : qUnion([Q0, Q1]), "operationType" : NewBodyOperationType.ADD, "oppositeDirection" : true, "depth" : 4 * mm});
        }
        {
            var Q0;
            Q0=makeQuery(id+"F23.boolean.opBoolean","COPY",EDGE,{"derivedFrom":makeQuery(id+"F23.opExtrude","CAP_EDGE",EDGE,{"disambiguationData":[OSD([sQuery(id+"F22.wireOp",EDGE,"E19.sketch_text.stroke-4")])],"isStart":true})});
            var Q1;
            Q1=makeQuery(id+"F23.boolean.opBoolean","COPY",EDGE,{"derivedFrom":makeQuery(id+"F23.opExtrude","CAP_EDGE",EDGE,{"disambiguationData":[OSD([sQuery(id+"F22.wireOp",EDGE,"E19.sketch_text.stroke-5")])],"isStart":true})});
            var Q2;
            Q2=makeQuery(id+"F23.boolean.opBoolean","COPY",EDGE,{"derivedFrom":makeQuery(id+"F23.opExtrude","CAP_EDGE",EDGE,{"disambiguationData":[OSD([sQuery(id+"F22.wireOp",EDGE,"E19.sketch_text.stroke-1")])],"isStart":true})});
            var Q3;
            Q3=makeQuery(id+"F23.boolean.opBoolean","COPY",EDGE,{"derivedFrom":makeQuery(id+"F23.opExtrude","CAP_EDGE",EDGE,{"disambiguationData":[OSD([sQuery(id+"F22.wireOp",EDGE,"E19.sketch_text.stroke-0")])],"isStart":true})});
            var Q4;
            Q4=makeQuery(id+"F23.boolean.opBoolean","COPY",EDGE,{"derivedFrom":makeQuery(id+"F23.opExtrude","CAP_EDGE",EDGE,{"disambiguationData":[OSD([sQuery(id+"F22.wireOp",EDGE,"E19.sketch_text.stroke-9")])],"isStart":true})});
            var Q5;
            Q5=makeQuery(id+"F23.boolean.opBoolean","COPY",EDGE,{"derivedFrom":makeQuery(id+"F23.opExtrude","CAP_EDGE",EDGE,{"disambiguationData":[OSD([sQuery(id+"F22.wireOp",EDGE,"E19.sketch_text.stroke-8")])],"isStart":true})});
            var Q6;
            Q6=makeQuery(id+"F23.boolean.opBoolean","COPY",EDGE,{"derivedFrom":makeQuery(id+"F23.opExtrude","CAP_EDGE",EDGE,{"disambiguationData":[OSD([sQuery(id+"F22.wireOp",EDGE,"E19.sketch_text.stroke-7")])],"isStart":true})});
            var Q7;
            Q7=makeQuery(id+"F23.boolean.opBoolean","COPY",EDGE,{"derivedFrom":makeQuery(id+"F23.opExtrude","CAP_EDGE",EDGE,{"disambiguationData":[OSD([sQuery(id+"F22.wireOp",EDGE,"E19.sketch_text.stroke-6")])],"isStart":true})});
            var Q8;
            Q8=makeQuery(id+"F23.boolean.opBoolean","COPY",EDGE,{"derivedFrom":makeQuery(id+"F23.opExtrude","CAP_EDGE",EDGE,{"disambiguationData":[OSD([sQuery(id+"F22.wireOp",EDGE,"E19.sketch_text.stroke-2")])],"isStart":true})});
            var Q9;
            Q9=makeQuery(id+"F23.boolean.opBoolean","COPY",EDGE,{"derivedFrom":makeQuery(id+"F23.opExtrude","CAP_EDGE",EDGE,{"disambiguationData":[OSD([sQuery(id+"F22.wireOp",EDGE,"E19.sketch_text.stroke-3")])],"isStart":true})});
            var Q10;
            Q10=makeQuery(id+"F23.boolean.opBoolean","COPY",EDGE,{"derivedFrom":makeQuery(id+"F23.opExtrude","CAP_EDGE",EDGE,{"disambiguationData":[OSD([sQuery(id+"F22.wireOp",EDGE,"E19.sketch_text.stroke-16")])],"isStart":true})});
            var Q11;
            {var subQ0=sQuery(id+"F24.wireOp",EDGE,"E21.left");Q11=makeQuery(id+"F25.opExtrude","CAP_EDGE",EDGE,{"disambiguationData":[OSD([subQ0]),TDD([makeQuery(id+"F24.imprint","IMPRINT",EDGE,{"disambiguationData":[TD([[makeQuery(id+"F24.imprint","INTERSECT",VERTEX,{"derivedFrom":[sQuery(id+"F24.wireOp",EDGE,"E21.bottom"),subQ0]}),-1.0]])],"derivedFrom":subQ0})])],"isStart":true});}
            var Q12;
            {var subQ0=sQuery(id+"F24.wireOp",EDGE,"E21.left");Q12=makeQuery(id+"F25.opExtrude","CAP_EDGE",EDGE,{"disambiguationData":[OSD([subQ0]),TDD([makeQuery(id+"F24.imprint","IMPRINT",EDGE,{"disambiguationData":[TD([[makeQuery(id+"F24.imprint","INTERSECT",VERTEX,{"derivedFrom":[sQuery(id+"F24.wireOp",EDGE,"E21.top"),subQ0]}),1.0]])],"derivedFrom":subQ0})])],"isStart":true});}
            var Q13;
            {var subQ0=sQuery(id+"F24.wireOp",EDGE,"E21.right");Q13=makeQuery(id+"F25.opExtrude","CAP_EDGE",EDGE,{"disambiguationData":[OSD([subQ0]),TDD([makeQuery(id+"F24.imprint","IMPRINT",EDGE,{"disambiguationData":[TD([[makeQuery(id+"F24.imprint","INTERSECT",VERTEX,{"derivedFrom":[sQuery(id+"F24.wireOp",EDGE,"E21.top"),subQ0]}),1.0]])],"derivedFrom":subQ0})])],"isStart":true});}
            var Q14;
            Q14=makeQuery(id+"F23.boolean.opBoolean","COPY",EDGE,{"derivedFrom":makeQuery(id+"F23.opExtrude","CAP_EDGE",EDGE,{"disambiguationData":[OSD([sQuery(id+"F22.wireOp",EDGE,"E19.sketch_text.stroke-11")])],"isStart":true})});
            var Q15;
            {var subQ0=sQuery(id+"F24.wireOp",EDGE,"E21.right");Q15=makeQuery(id+"F25.opExtrude","CAP_EDGE",EDGE,{"disambiguationData":[OSD([subQ0]),TDD([makeQuery(id+"F24.imprint","IMPRINT",EDGE,{"disambiguationData":[TD([[makeQuery(id+"F24.imprint","INTERSECT",VERTEX,{"derivedFrom":[sQuery(id+"F24.wireOp",EDGE,"E21.bottom"),subQ0]}),-1.0]])],"derivedFrom":subQ0})])],"isStart":true});}
            var Q16;
            Q16=makeQuery(id+"F23.boolean.opBoolean","COPY",EDGE,{"derivedFrom":makeQuery(id+"F23.opExtrude","CAP_EDGE",EDGE,{"disambiguationData":[OSD([sQuery(id+"F22.wireOp",EDGE,"E19.sketch_text.stroke-29")])],"isStart":true})});
            var Q17;
            Q17=makeQuery(id+"F23.boolean.opBoolean","COPY",EDGE,{"derivedFrom":makeQuery(id+"F23.opExtrude","CAP_EDGE",EDGE,{"disambiguationData":[OSD([sQuery(id+"F22.wireOp",EDGE,"E19.sketch_text.stroke-24")])],"isStart":true})});
            var Q18;
            Q18=makeQuery(id+"F23.boolean.opBoolean","COPY",EDGE,{"derivedFrom":makeQuery(id+"F23.opExtrude","CAP_EDGE",EDGE,{"disambiguationData":[OSD([sQuery(id+"F22.wireOp",EDGE,"E19.sketch_text.stroke-37")])],"isStart":true})});
            var Q19;
            Q19=makeQuery(id+"F23.boolean.opBoolean","COPY",EDGE,{"derivedFrom":makeQuery(id+"F23.opExtrude","CAP_EDGE",EDGE,{"disambiguationData":[OSD([sQuery(id+"F22.wireOp",EDGE,"E19.sketch_text.stroke-52")])],"isStart":true})});
            var Q20;
            Q20=makeQuery(id+"F23.boolean.opBoolean","COPY",EDGE,{"derivedFrom":makeQuery(id+"F23.opExtrude","CAP_EDGE",EDGE,{"disambiguationData":[OSD([sQuery(id+"F22.wireOp",EDGE,"E19.sketch_text.stroke-56")])],"isStart":true})});
            var Q21;
            Q21=makeQuery(id+"F23.boolean.opBoolean","COPY",EDGE,{"derivedFrom":makeQuery(id+"F23.opExtrude","CAP_EDGE",EDGE,{"disambiguationData":[OSD([sQuery(id+"F22.wireOp",EDGE,"E19.sketch_text.stroke-32")])],"isStart":true})});
            var Q22;
            Q22=makeQuery(id+"F23.boolean.opBoolean","COPY",EDGE,{"derivedFrom":makeQuery(id+"F23.opExtrude","CAP_EDGE",EDGE,{"disambiguationData":[OSD([sQuery(id+"F22.wireOp",EDGE,"E19.sketch_text.stroke-42")])],"isStart":true})});
            var Q23;
            Q23=makeQuery(id+"F23.boolean.opBoolean","COPY",EDGE,{"derivedFrom":makeQuery(id+"F23.opExtrude","CAP_EDGE",EDGE,{"disambiguationData":[OSD([sQuery(id+"F22.wireOp",EDGE,"E19.sketch_text.stroke-48")])],"isStart":true})});
            var Q24;
            Q24=makeQuery(id+"F23.boolean.opBoolean","COPY",EDGE,{"derivedFrom":makeQuery(id+"F23.opExtrude","CAP_EDGE",EDGE,{"disambiguationData":[OSD([sQuery(id+"F22.wireOp",EDGE,"E19.sketch_text.stroke-91")])],"isStart":true})});
            var Q25;
            Q25=makeQuery(id+"F23.boolean.opBoolean","COPY",EDGE,{"derivedFrom":makeQuery(id+"F23.opExtrude","CAP_EDGE",EDGE,{"disambiguationData":[OSD([sQuery(id+"F22.wireOp",EDGE,"E19.sketch_text.stroke-63")])],"isStart":true})});
            var Q26;
            Q26=makeQuery(id+"F23.boolean.opBoolean","COPY",EDGE,{"derivedFrom":makeQuery(id+"F23.opExtrude","CAP_EDGE",EDGE,{"disambiguationData":[OSD([sQuery(id+"F22.wireOp",EDGE,"E19.sketch_text.stroke-87")])],"isStart":true})});
            var Q27;
            Q27=makeQuery(id+"F23.boolean.opBoolean","COPY",EDGE,{"derivedFrom":makeQuery(id+"F23.opExtrude","CAP_EDGE",EDGE,{"disambiguationData":[OSD([sQuery(id+"F22.wireOp",EDGE,"E19.sketch_text.stroke-78")])],"isStart":true})});
            var Q28;
            Q28=makeQuery(id+"F23.boolean.opBoolean","COPY",EDGE,{"derivedFrom":makeQuery(id+"F23.opExtrude","CAP_EDGE",EDGE,{"disambiguationData":[OSD([sQuery(id+"F22.wireOp",EDGE,"E19.sketch_text.stroke-73")])],"isStart":true})});
            var Q29;
            Q29=makeQuery(id+"F23.boolean.opBoolean","COPY",EDGE,{"derivedFrom":makeQuery(id+"F23.opExtrude","CAP_EDGE",EDGE,{"disambiguationData":[OSD([sQuery(id+"F22.wireOp",EDGE,"E19.sketch_text.stroke-83")])],"isStart":true})});
            var Q30;
            Q30=makeQuery(id+"F23.boolean.opBoolean","COPY",EDGE,{"derivedFrom":makeQuery(id+"F23.opExtrude","CAP_EDGE",EDGE,{"disambiguationData":[OSD([sQuery(id+"F22.wireOp",EDGE,"E19.sketch_text.stroke-68")])],"isStart":true})});
            var Q31;
            Q31=makeQuery(id+"F23.boolean.opBoolean","COPY",EDGE,{"derivedFrom":makeQuery(id+"F23.opExtrude","CAP_EDGE",EDGE,{"disambiguationData":[OSD([sQuery(id+"F22.wireOp",EDGE,"E19.sketch_text.stroke-70")])],"isStart":true})});
            var Q32;
            Q32=makeQuery(id+"F23.boolean.opBoolean","COPY",EDGE,{"derivedFrom":makeQuery(id+"F23.opExtrude","CAP_EDGE",EDGE,{"disambiguationData":[OSD([sQuery(id+"F22.wireOp",EDGE,"E19.sketch_text.stroke-102")])],"isStart":true})});
            var Q33;
            Q33=makeQuery(id+"F23.boolean.opBoolean","COPY",EDGE,{"derivedFrom":makeQuery(id+"F23.opExtrude","CAP_EDGE",EDGE,{"disambiguationData":[OSD([sQuery(id+"F22.wireOp",EDGE,"E19.sketch_text.stroke-101")])],"isStart":true})});
            var Q34;
            Q34=makeQuery(id+"F23.boolean.opBoolean","COPY",EDGE,{"derivedFrom":makeQuery(id+"F23.opExtrude","CAP_EDGE",EDGE,{"disambiguationData":[OSD([sQuery(id+"F22.wireOp",EDGE,"E19.sketch_text.stroke-99")])],"isStart":true})});
            var Q35;
            Q35=makeQuery(id+"F23.boolean.opBoolean","COPY",EDGE,{"derivedFrom":makeQuery(id+"F23.opExtrude","CAP_EDGE",EDGE,{"disambiguationData":[OSD([sQuery(id+"F22.wireOp",EDGE,"E19.sketch_text.stroke-100")])],"isStart":true})});
            var Q36;
            Q36=makeQuery(id+"F23.boolean.opBoolean","COPY",EDGE,{"derivedFrom":makeQuery(id+"F23.opExtrude","CAP_EDGE",EDGE,{"disambiguationData":[OSD([sQuery(id+"F22.wireOp",EDGE,"E19.sketch_text.stroke-103")])],"isStart":true})});
            var Q37;
            Q37=makeQuery(id+"F23.boolean.opBoolean","COPY",EDGE,{"derivedFrom":makeQuery(id+"F23.opExtrude","CAP_EDGE",EDGE,{"disambiguationData":[OSD([sQuery(id+"F22.wireOp",EDGE,"E19.sketch_text.stroke-97")])],"isStart":true})});
            var Q38;
            Q38=makeQuery(id+"F23.boolean.opBoolean","COPY",EDGE,{"derivedFrom":makeQuery(id+"F23.opExtrude","CAP_EDGE",EDGE,{"disambiguationData":[OSD([sQuery(id+"F22.wireOp",EDGE,"E19.sketch_text.stroke-96")])],"isStart":true})});
            var Q39;
            Q39=makeQuery(id+"F23.boolean.opBoolean","COPY",EDGE,{"derivedFrom":makeQuery(id+"F23.opExtrude","CAP_EDGE",EDGE,{"disambiguationData":[OSD([sQuery(id+"F22.wireOp",EDGE,"E19.sketch_text.stroke-104")])],"isStart":true})});
            var Q40;
            Q40=makeQuery(id+"F23.boolean.opBoolean","COPY",EDGE,{"derivedFrom":makeQuery(id+"F23.opExtrude","CAP_EDGE",EDGE,{"disambiguationData":[OSD([sQuery(id+"F22.wireOp",EDGE,"E19.sketch_text.stroke-92")])],"isStart":true})});
            var Q41;
            Q41=makeQuery(id+"F23.boolean.opBoolean","COPY",EDGE,{"derivedFrom":makeQuery(id+"F23.opExtrude","CAP_EDGE",EDGE,{"disambiguationData":[OSD([sQuery(id+"F22.wireOp",EDGE,"E19.sketch_text.stroke-94")])],"isStart":true})});
            var Q42;
            Q42=makeQuery(id+"F23.boolean.opBoolean","COPY",EDGE,{"derivedFrom":makeQuery(id+"F23.opExtrude","CAP_EDGE",EDGE,{"disambiguationData":[OSD([sQuery(id+"F22.wireOp",EDGE,"E19.sketch_text.stroke-95")])],"isStart":true})});
            var Q43;
            Q43=makeQuery(id+"F23.boolean.opBoolean","COPY",EDGE,{"derivedFrom":makeQuery(id+"F23.opExtrude","CAP_EDGE",EDGE,{"disambiguationData":[OSD([sQuery(id+"F22.wireOp",EDGE,"E19.sketch_text.stroke-60")])],"isStart":true})});
            chamfer(context, id + "F26", {"entities" : qUnion([Q0, Q1, Q2, Q3, Q4, Q5, Q6, Q7, Q8, Q9, Q10, Q11, Q12, Q13, Q14, Q15, Q16, Q17, Q18, Q19, Q20, Q21, Q22, Q23, Q24, Q25, Q26, Q27, Q28, Q29, Q30, Q31, Q32, Q33, Q34, Q35, Q36, Q37, Q38, Q39, Q40, Q41, Q42, Q43]), "chamferType" : ChamferType.OFFSET_ANGLE, "width" : .6 * mm, "oppositeDirection" : false, "angle" : 45 * degree, "tangentPropagation" : true});
        }
    });
